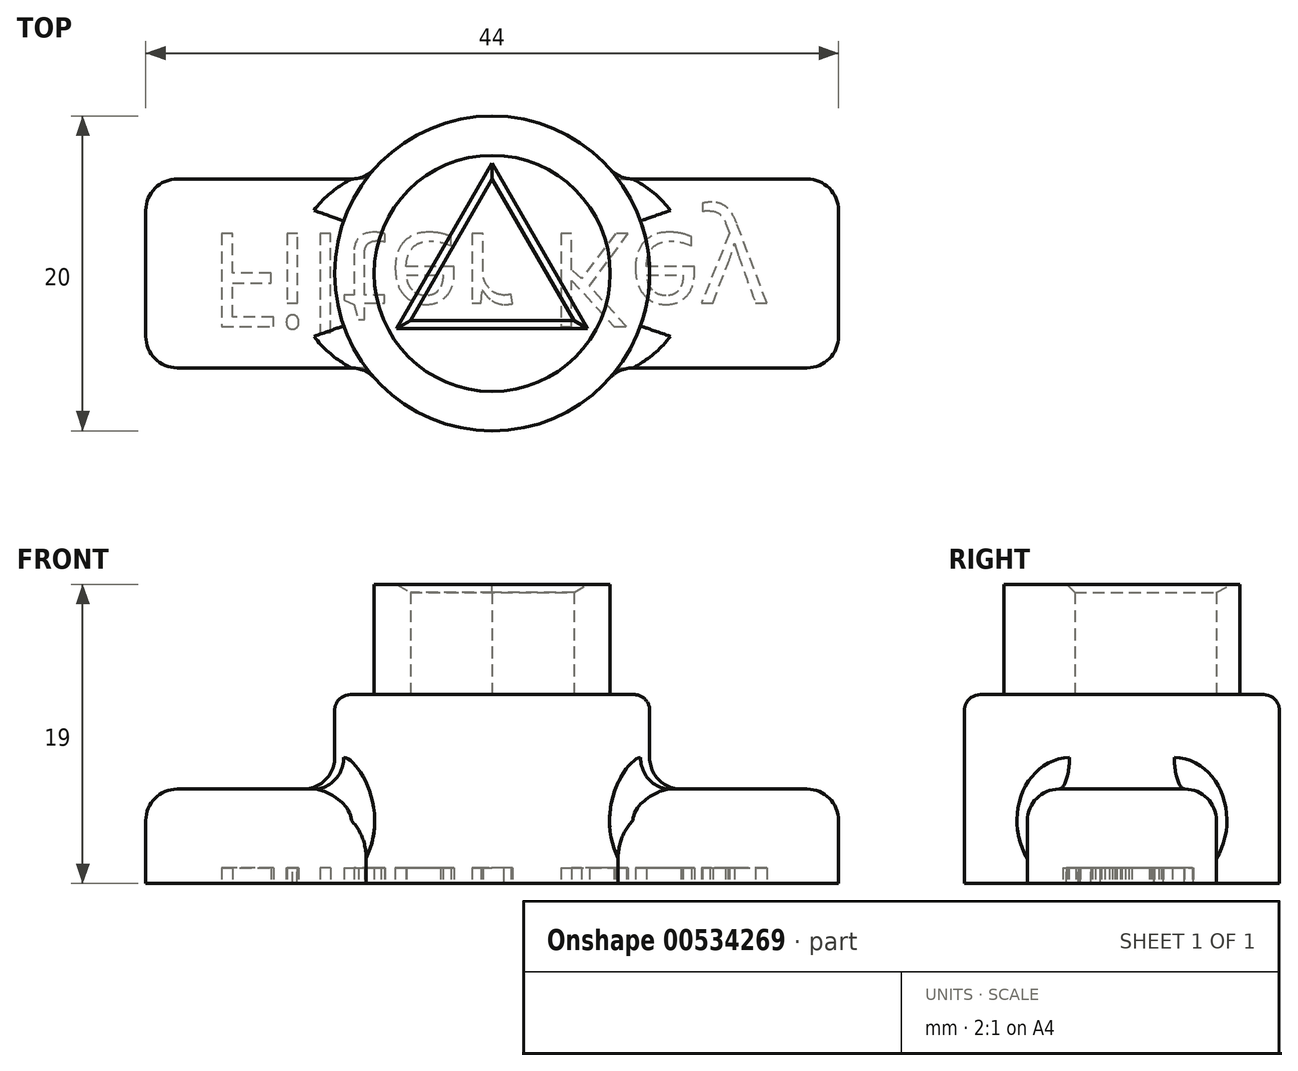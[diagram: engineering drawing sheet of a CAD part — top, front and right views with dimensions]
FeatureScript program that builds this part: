
annotation { "Feature Type Name" : "Feature", "Feature Type Description" : "" }
export const myFeature = defineFeature(function(context is Context, id is Id, definition is map)
    precondition{}
    {
        {
            var Q0;
            Q0=qCreatedBy(makeId("Top.planeOp"),FACE);
            var sketch = newSketch(context, id + "F0", { "sketchPlane" : qUnion([Q0])});
            skCircle(sketch, "E0", {"center": v(0, 0) * mm, "radius": 7.5 * mm});
            skCircle(sketch, "E1", {"center": v(0, 0) * mm, "radius": 10 * mm});
            skCircle(sketch, "E2.cCircle", {"center": v(0, 0) * mm, "radius": 6 * mm, "construction": true});
            skLineSegment(sketch, "E2.0", {"start": v(5.2, -3) * mm, "end": v(-5.2, -3) * mm});
            skLineSegment(sketch, "E2.1", {"start": v(-5.2, -3) * mm, "end": v(0, 6) * mm});
            skLineSegment(sketch, "E2.2", {"start": v(0, 6) * mm, "end": v(5.2, -3) * mm});
            skSolve(sketch);
        }
        {
            var Q0;
            Q0 = qSketchRegion(id + "F0", true);
            var Q1;
            Q1=makeQuery(id+"F0.imprint","IMPRINT",FACE,{"disambiguationData":[TD([[makeQuery(id+"F0.imprint","IMPRINT",EDGE,{"derivedFrom":sQuery(id+"F0.wireOp",EDGE,"E2.0")}),-1.0]])]});
            var Q2;
            Q2=makeQuery(id+"F0.imprint","IMPRINT",FACE,{"disambiguationData":[TD([[makeQuery(id+"F0.imprint","IMPRINT",EDGE,{"derivedFrom":sQuery(id+"F0.wireOp",EDGE,"E0")}),1.0]])]});
            extrude(context, id + "F1", {"entities" : qUnion([Q0, Q1, Q2]), "oppositeDirection" : true, "depth" : 12 * mm, "offsetDistance" : 25 * mm});
        }
        {
            var Q0;
            Q0=makeQuery(id+"F0.imprint","IMPRINT",FACE,{"disambiguationData":[TD([[makeQuery(id+"F0.imprint","IMPRINT",EDGE,{"derivedFrom":sQuery(id+"F0.wireOp",EDGE,"E0")}),1.0]])]});
            extrude(context, id + "F2", {"entities" : qUnion([Q0]), "operationType" : NewBodyOperationType.ADD, "depth" : 7 * mm, "offsetDistance" : 25 * mm});
        }
        {
            var Q0;
            Q0=makeQuery(id+"F1.opExtrude","CAP_FACE",FACE,{"disambiguationData":[OSD([sQuery(id+"F0.wireOp",EDGE,"E1")])],"isStart":false});
            var sketch = newSketch(context, id + "F3", { "sketchPlane" : qUnion([Q0])});
            skLineSegment(sketch, "E3.bottom", {"start": v(22, -6) * mm, "end": v(-22, -6) * mm});
            skLineSegment(sketch, "E3.top", {"start": v(22, 6) * mm, "end": v(-22, 6) * mm});
            skLineSegment(sketch, "E3.left", {"start": v(22, -6) * mm, "end": v(22, 6) * mm});
            skLineSegment(sketch, "E3.right", {"start": v(-22, -6) * mm, "end": v(-22, 6) * mm});
            skPoint(sketch, "E3.middle", {"position": v(0, 0) * mm});
            skSolve(sketch);
        }
        {
            var Q0;
            Q0 = qSketchRegion(id + "F3", true);
            extrude(context, id + "F4", {"entities" : qUnion([Q0]), "operationType" : NewBodyOperationType.ADD, "oppositeDirection" : true, "depth" : 6 * mm, "offsetDistance" : 25 * mm});
        }
        {
            var Q0;
            Q0=makeQuery(id+"F4.boolean.opBoolean","INTERSECT",EDGE,{"disambiguationData":[OD(1.0)],"derivedFrom":[makeQuery(id+"F1.opExtrude","SWEPT_FACE",FACE,{"disambiguationData":[OSD([sQuery(id+"F0.wireOp",EDGE,"E1")])]}),makeQuery(id+"F4.opExtrude","CAP_FACE",FACE,{"disambiguationData":[OSD([sQuery(id+"F3.wireOp",EDGE,"E3.bottom"),sQuery(id+"F3.wireOp",EDGE,"E3.top"),sQuery(id+"F3.wireOp",EDGE,"E3.left"),sQuery(id+"F3.wireOp",EDGE,"E3.right")])],"isStart":false})]});
            var Q1;
            Q1=makeQuery(id+"F4.boolean.opBoolean","INTERSECT",EDGE,{"disambiguationData":[OD(0.0)],"derivedFrom":[makeQuery(id+"F1.opExtrude","SWEPT_FACE",FACE,{"disambiguationData":[OSD([sQuery(id+"F0.wireOp",EDGE,"E1")])]}),makeQuery(id+"F4.opExtrude","CAP_FACE",FACE,{"disambiguationData":[OSD([sQuery(id+"F3.wireOp",EDGE,"E3.bottom"),sQuery(id+"F3.wireOp",EDGE,"E3.top"),sQuery(id+"F3.wireOp",EDGE,"E3.left"),sQuery(id+"F3.wireOp",EDGE,"E3.right")])],"isStart":false})]});
            var Q2;
            Q2=makeQuery(id+"F4.opExtrude","SWEPT_EDGE",EDGE,{"disambiguationData":[OSD([sQuery(id+"F3.wireOp",EDGE,"E3.top"),sQuery(id+"F3.wireOp",EDGE,"E3.left")])]});
            var Q3;
            Q3=makeQuery(id+"F4.opExtrude","SWEPT_EDGE",EDGE,{"disambiguationData":[OSD([sQuery(id+"F3.wireOp",EDGE,"E3.bottom"),sQuery(id+"F3.wireOp",EDGE,"E3.left")])]});
            var Q4;
            {var subQ0=sQuery(id+"F3.wireOp",EDGE,"E3.bottom");var subQ1=sQuery(id+"F3.wireOp",EDGE,"E3.top");var subQ2=sQuery(id+"F3.wireOp",EDGE,"E3.left");Q4=makeQuery(id+"F4.boolean.opBoolean","SPLIT",FACE,{"disambiguationData":[TD([makeQuery(id+"F4.opExtrude","SWEPT_FACE",FACE,{"disambiguationData":[OSD([subQ2])]})])],"derivedFrom":makeQuery(id+"F4.opExtrude","CAP_FACE",FACE,{"disambiguationData":[OSD([subQ0,subQ1,subQ2,sQuery(id+"F3.wireOp",EDGE,"E3.right")])],"isStart":false})});}
            var Q5;
            {var subQ0=sQuery(id+"F3.wireOp",EDGE,"E3.bottom");var subQ1=sQuery(id+"F3.wireOp",EDGE,"E3.right");var subQ2=sQuery(id+"F3.wireOp",EDGE,"E3.top");Q5=makeQuery(id+"F4.boolean.opBoolean","SPLIT",FACE,{"disambiguationData":[TD([makeQuery(id+"F4.opExtrude","SWEPT_FACE",FACE,{"disambiguationData":[OSD([subQ1])]})])],"derivedFrom":makeQuery(id+"F4.opExtrude","CAP_FACE",FACE,{"disambiguationData":[OSD([subQ0,subQ2,sQuery(id+"F3.wireOp",EDGE,"E3.left"),subQ1])],"isStart":false})});}
            var Q6;
            Q6=makeQuery(id+"F4.opExtrude","SWEPT_EDGE",EDGE,{"disambiguationData":[OSD([sQuery(id+"F3.wireOp",EDGE,"E3.top"),sQuery(id+"F3.wireOp",EDGE,"E3.right")])]});
            var Q7;
            Q7=makeQuery(id+"F4.opExtrude","SWEPT_EDGE",EDGE,{"disambiguationData":[OSD([sQuery(id+"F3.wireOp",EDGE,"E3.bottom"),sQuery(id+"F3.wireOp",EDGE,"E3.right")])]});
            fillet(context, id + "F5", {"entities" : qUnion([Q0, Q1, Q2, Q3, Q4, Q5, Q6, Q7]), "radius" : 2 * mm, "tangentPropagation" : true, "allowEdgeOverflow" : false});
        }
        {
            var Q0;
            Q0=makeQuery(id+"F1.opExtrude","CAP_EDGE",EDGE,{"disambiguationData":[OSD([sQuery(id+"F0.wireOp",EDGE,"E1")])],"isStart":true});
            fillet(context, id + "F6", {"entities" : qUnion([Q0]), "radius" : 1 * mm, "tangentPropagation" : true, "allowEdgeOverflow" : false});
        }
        {
            var Q0;
            Q0=makeQuery(id+"F4.boolean.opBoolean","MERGE",FACE,{"derivedFrom":[makeQuery(id+"F1.opExtrude","CAP_FACE",FACE,{"disambiguationData":[OSD([sQuery(id+"F0.wireOp",EDGE,"E1")])],"isStart":false}),makeQuery(id+"F4.opExtrude","CAP_FACE",FACE,{"disambiguationData":[OSD([sQuery(id+"F3.wireOp",EDGE,"E3.bottom"),sQuery(id+"F3.wireOp",EDGE,"E3.top"),sQuery(id+"F3.wireOp",EDGE,"E3.left"),sQuery(id+"F3.wireOp",EDGE,"E3.right")])],"isStart":true})]});
            var sketch = newSketch(context, id + "F7", { "sketchPlane" : qUnion([Q0])});
            skText(sketch, "E4", { "text": "Filter Key", "fontName": "OpenSans-Regular.ttf"});
            const initialGuessF7  = {"E4": [-0.018, -0.00254, 1, 0, 0.00596]};
            skSetInitialGuess(sketch, initialGuessF7);
            skSolve(sketch);
        }
        {
            var Q0;
            Q0 = qSketchRegion(id + "F7", true);
            extrude(context, id + "F8", {"entities" : qUnion([Q0]), "operationType" : NewBodyOperationType.REMOVE, "oppositeDirection" : true, "depth" : 1 * mm, "offsetDistance" : 25 * mm});
        }
        {
            var Q0;
            Q0=makeQuery(id+"F2.opExtrude","CAP_EDGE",EDGE,{"disambiguationData":[OSD([sQuery(id+"F0.wireOp",EDGE,"E2.1")])],"isStart":false});
            var Q1;
            Q1=makeQuery(id+"F2.opExtrude","CAP_EDGE",EDGE,{"disambiguationData":[OSD([sQuery(id+"F0.wireOp",EDGE,"E2.2")])],"isStart":false});
            var Q2;
            Q2=makeQuery(id+"F2.opExtrude","CAP_EDGE",EDGE,{"disambiguationData":[OSD([sQuery(id+"F0.wireOp",EDGE,"E2.0")])],"isStart":false});
            chamfer(context, id + "F9", {"entities" : qUnion([Q0, Q1, Q2]), "width" : 0.5 * mm, "tangentPropagation" : true});
        }
    });
